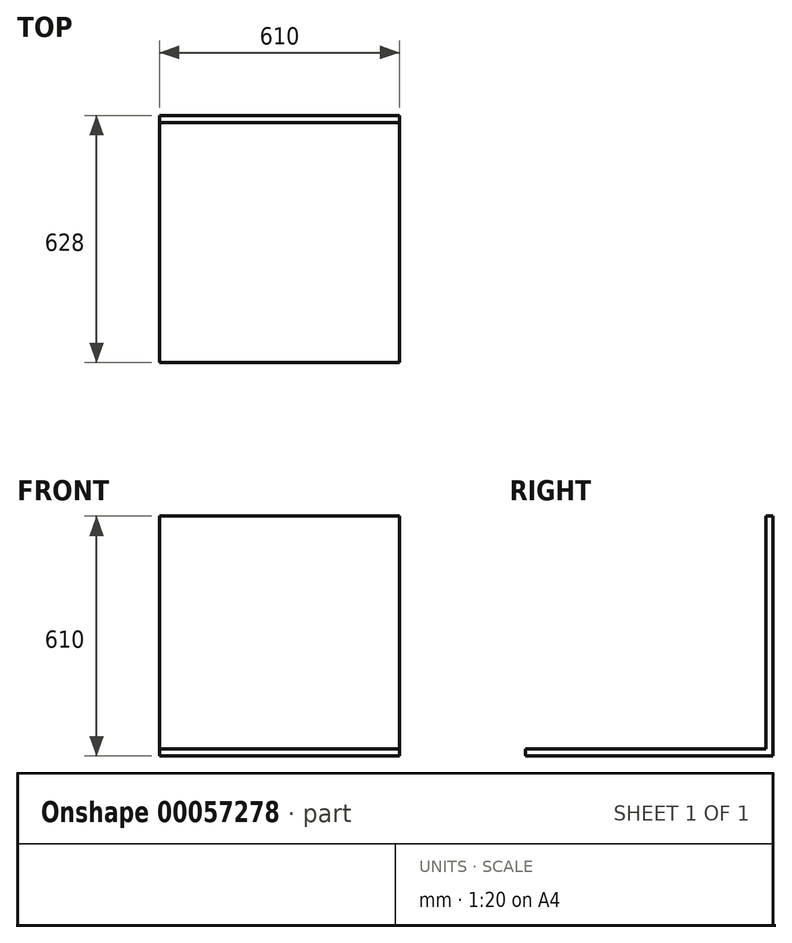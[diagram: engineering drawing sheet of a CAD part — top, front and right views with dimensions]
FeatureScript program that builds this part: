
annotation { "Feature Type Name" : "Feature", "Feature Type Description" : "" }
export const myFeature = defineFeature(function(context is Context, id is Id, definition is map)
    precondition{}
    {
        {
            var Q0;
            Q0=qCreatedBy(makeId("Top.planeOp"),FACE);
            var sketch = newSketch(context, id + "F0", { "sketchPlane" : qUnion([Q0])});
            skLineSegment(sketch, "E0.rect.bottom", {"start": v(-305, 305) * mm, "end": v(305, 305) * mm});
            skLineSegment(sketch, "E0.rect.top", {"start": v(-305, -305) * mm, "end": v(305, -305) * mm});
            skLineSegment(sketch, "E0.rect.left", {"start": v(-305, 305) * mm, "end": v(-305, -305) * mm});
            skLineSegment(sketch, "E0.rect.right", {"start": v(305, 305) * mm, "end": v(305, -305) * mm});
            skPoint(sketch, "E0.rect.middle", {"position": v(0, 0) * mm});
            skSolve(sketch);
        }
        {
            var Q0;
            Q0=makeQuery(id+"F0.imprint","IMPRINT",FACE,{"disambiguationData":[TD([[makeQuery(id+"F0.imprint","IMPRINT",EDGE,{"derivedFrom":sQuery(id+"F0.wireOp",EDGE,"E0.rect.bottom")}),-1.0]])]});
            extrude(context, id + "F1", {"entities" : qUnion([Q0]), "depth" : 18 * mm});
        }
        {
            var Q0;
            Q0=makeQuery(id+"F1.opExtrude","CAP_EDGE",EDGE,{"disambiguationData":[OSD([sQuery(id+"F0.wireOp",EDGE,"E0.rect.bottom")])],"isStart":false});
            cPlane(context, id + "F2", {"entities" : qUnion([Q0]), "cplaneType" : CPlaneType.LINE_ANGLE, "offset" : 150 * mm, "angle" : 0 * degree, "width" : 150 * mm, "height" : 150 * mm});
        }
        {
            var Q0;
            Q0=qCreatedBy(id+"F2.planeOp",FACE);
            var sketch = newSketch(context, id + "F3", { "sketchPlane" : qUnion([Q0])});
            skLineSegment(sketch, "E1.0", {"start": v(305, 0) * mm, "end": v(-305, 0) * mm});
            skLineSegment(sketch, "E2", {"start": v(305, 0) * mm, "end": v(305, 610) * mm});
            skLineSegment(sketch, "E3", {"start": v(305, 610) * mm, "end": v(-305, 610) * mm});
            skLineSegment(sketch, "E4", {"start": v(-305, 610) * mm, "end": v(-305, 0) * mm});
            skSolve(sketch);
        }
        {
            var Q0;
            Q0=makeQuery(id+"F3.imprint","IMPRINT",FACE,{"disambiguationData":[TD([[makeQuery(id+"F3.imprint","IMPRINT",EDGE,{"derivedFrom":sQuery(id+"F3.wireOp",EDGE,"E1.0")}),-1.0]])]});
            extrude(context, id + "F4", {"entities" : qUnion([Q0]), "operationType" : NewBodyOperationType.ADD, "depth" : 18 * mm});
        }
        {
            var Q0;
            Q0=makeQuery(id+"F4.boolean.opBoolean","MERGE",EDGE,{"derivedFrom":[makeQuery(id+"F1.opExtrude","CAP_EDGE",EDGE,{"disambiguationData":[OSD([sQuery(id+"F0.wireOp",EDGE,"E0.rect.right")])],"isStart":true}),makeQuery(id+"F4.opExtrude","SWEPT_EDGE",EDGE,{"disambiguationData":[OSD([sQuery(id+"F3.wireOp",EDGE,"E1.0"),sQuery(id+"F3.wireOp",EDGE,"E4")])]})]});
            cPlane(context, id + "F5", {"entities" : qUnion([Q0]), "cplaneType" : CPlaneType.LINE_ANGLE, "offset" : 150 * mm, "angle" : 90 * degree, "flipAlignment" : true, "width" : 150 * mm, "height" : 150 * mm});
        }
    });
